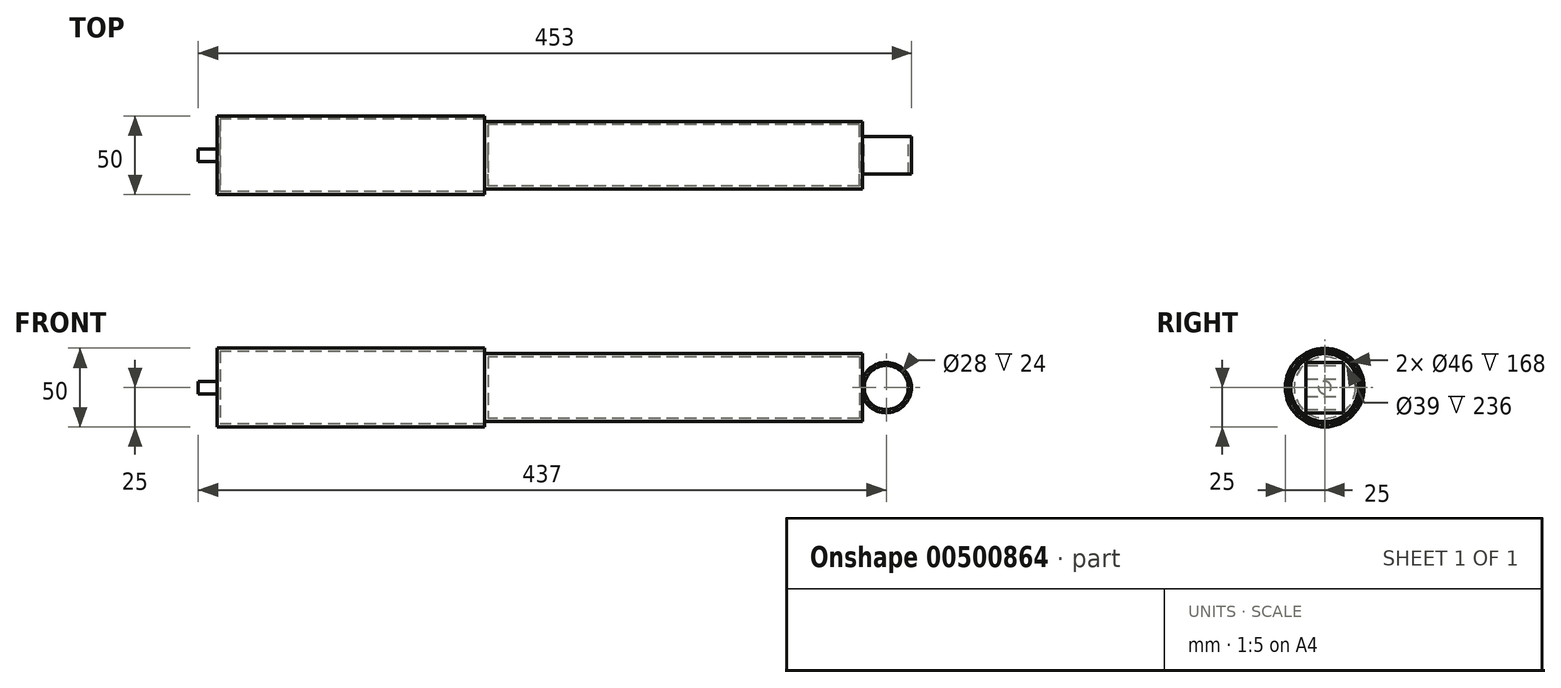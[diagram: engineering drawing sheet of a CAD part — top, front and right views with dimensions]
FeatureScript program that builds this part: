
annotation { "Feature Type Name" : "Feature", "Feature Type Description" : "" }
export const myFeature = defineFeature(function(context is Context, id is Id, definition is map)
    precondition{}
    {
        {
            var Q0;
            Q0=qCreatedBy(makeId("Front.planeOp"),FACE);
            var sketch = newSketch(context, id + "F0", { "sketchPlane" : qUnion([Q0])});
            skLineSegment(sketch, "E0", {"start": v(0, 0) * mm, "end": v(500, 0) * mm, "construction": true});
            skLineSegment(sketch, "E1", {"start": v(0, 0) * mm, "end": v(0, 4) * mm});
            skLineSegment(sketch, "E2", {"start": v(0, 4) * mm, "end": v(12, 4) * mm});
            skLineSegment(sketch, "E3", {"start": v(12, 4) * mm, "end": v(12, 0) * mm});
            skLineSegment(sketch, "E4", {"start": v(12, 0) * mm, "end": v(12, 25) * mm});
            skLineSegment(sketch, "E5", {"start": v(12, 25) * mm, "end": v(182, 25) * mm});
            skLineSegment(sketch, "E6", {"start": v(182, 25) * mm, "end": v(182, 0) * mm});
            skLineSegment(sketch, "E7", {"start": v(182, 23) * mm, "end": v(12, 23) * mm});
            skLineSegment(sketch, "E8", {"start": v(0, 0) * mm, "end": v(12, 0) * mm});
            skLineSegment(sketch, "E9", {"start": v(14, 0) * mm, "end": v(14, 23) * mm});
            skLineSegment(sketch, "E10", {"start": v(12, 0) * mm, "end": v(14, 0) * mm});
            skLineSegment(sketch, "E11", {"start": v(182, 0) * mm, "end": v(182, 21.5) * mm});
            skLineSegment(sketch, "E12", {"start": v(182, 21.5) * mm, "end": v(422, 21.5) * mm});
            skLineSegment(sketch, "E13", {"start": v(422, 21.5) * mm, "end": v(422, 0) * mm});
            skLineSegment(sketch, "E14", {"start": v(422, 19.5) * mm, "end": v(182, 19.5) * mm});
            skLineSegment(sketch, "E15", {"start": v(182, 0) * mm, "end": v(184, 0) * mm});
            skLineSegment(sketch, "E16", {"start": v(184, 0) * mm, "end": v(184, 19.5) * mm});
            skLineSegment(sketch, "E17", {"start": v(184, 7) * mm, "end": v(182, 7) * mm});
            skLineSegment(sketch, "E18", {"start": v(420, 0) * mm, "end": v(420, 19.5) * mm});
            skLineSegment(sketch, "E19", {"start": v(420, 0) * mm, "end": v(422, 0) * mm});
            skSolve(sketch);
        }
        {
            var Q0;
            Q0=qSketchRegion(id+"F0",true);
            var Q1;
            Q1=sQuery(id+"F0.wireOp",EDGE,"E0");
            revolve(context, id + "F1", {"entities" : qUnion([Q0]), "axis" : qUnion([Q1]), "revolveType" : RevolveType.FULL});
        }
        {
            var Q0;
            Q0=qCreatedBy(makeId("Front.planeOp"),FACE);
            var sketch = newSketch(context, id + "F2", { "sketchPlane" : qUnion([Q0])});
            skPoint(sketch, "E20", {"position": v(437, 0) * mm});
            skCircle(sketch, "E21", {"center": v(437, 0) * mm, "radius": 16 * mm});
            skCircle(sketch, "E22", {"center": v(437, 0) * mm, "radius": 14 * mm});
            skSolve(sketch);
        }
        {
            var Q0;
            Q0=qSketchRegion(id+"F2",true);
            extrude(context, id + "F3", {"entities" : qUnion([Q0]), "operationType" : NewBodyOperationType.ADD, "endBound" : BoundingType.SYMMETRIC, "offsetDistance" : 25 * mm, "depth" : 24 * mm});
        }
    });
